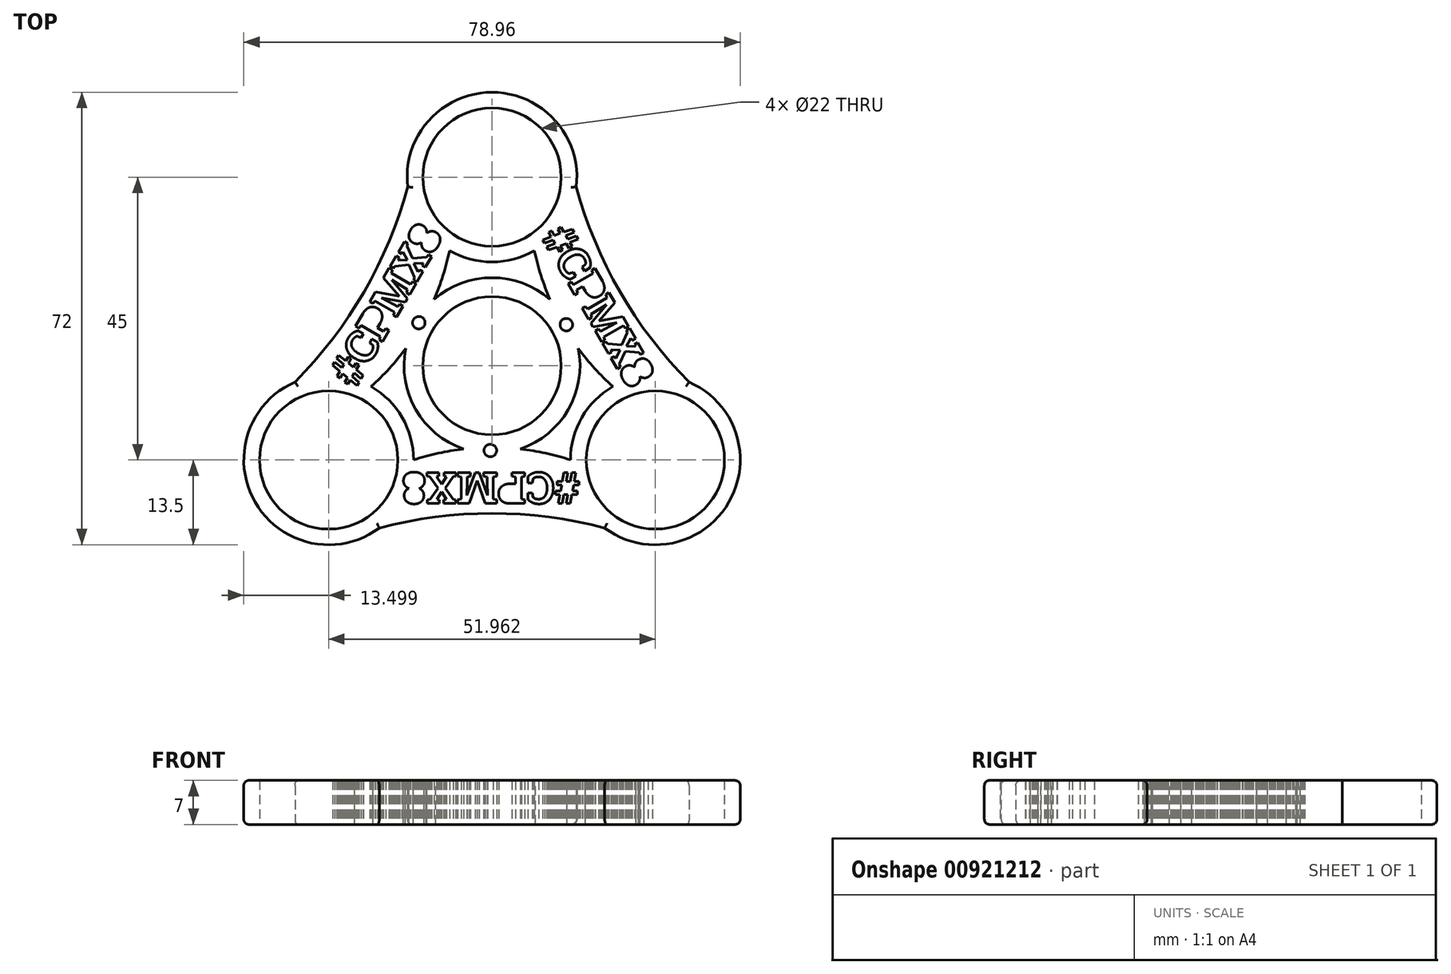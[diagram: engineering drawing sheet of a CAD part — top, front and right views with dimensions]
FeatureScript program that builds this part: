
annotation { "Feature Type Name" : "Feature", "Feature Type Description" : "" }
export const myFeature = defineFeature(function(context is Context, id is Id, definition is map)
    precondition{}
    {
        {
            var Q0;
            Q0=qCreatedBy(makeId("Top.planeOp"),FACE);
            var sketch = newSketch(context, id + "F0", { "sketchPlane" : qUnion([Q0])});
            skCircle(sketch, "E0", {"center": v(0, 0) * mm, "radius": 11 * mm});
            skLineSegment(sketch, "E1", {"start": v(0, 0) * mm, "end": v(0, 30) * mm, "construction": true});
            skCircle(sketch, "E2", {"center": v(0, 30) * mm, "radius": 11 * mm});
            skCircle(sketch, "E3.1.0", {"center": v(-25.98, -15) * mm, "radius": 11 * mm});
            skCircle(sketch, "E3.2.0", {"center": v(25.98, -15) * mm, "radius": 11 * mm});
            skArc(sketch, "E4.0", {"start": v(-31.34, -2.6) * mm, "mid": v(-37.67, -21.75) * mm, "end": v(-17.93, -25.83) * mm});
            skArc(sketch, "E5.0", {"start": v(-6.75, 18.3) * mm, "mid": v(0, 16.5) * mm, "end": v(6.75, 18.3) * mm});
            skArc(sketch, "E6.0", {"start": v(19.23, -3.3) * mm, "mid": v(14.29, -8.25) * mm, "end": v(12.48, -15) * mm});
            skArc(sketch, "E7.0", {"start": v(-13.73, 2.73) * mm, "mid": v(-12.12, -7) * mm, "end": v(-4.5, -13.26) * mm});
            skLineSegment(sketch, "E8", {"start": v(25.98, -15) * mm, "end": v(0, 30) * mm, "construction": true});
            skLineSegment(sketch, "E9", {"start": v(0, 30) * mm, "end": v(-25.98, -15) * mm, "construction": true});
            skArc(sketch, "E10", {"start": v(-31.34, -2.6) * mm, "mid": v(-20.35, 11.75) * mm, "end": v(-13.4, 28.44) * mm});
            skArc(sketch, "E11", {"start": v(17.93, -25.83) * mm, "mid": v(0, -23.5) * mm, "end": v(-17.93, -25.83) * mm});
            skArc(sketch, "E12", {"start": v(13.4, 28.44) * mm, "mid": v(20.35, 11.75) * mm, "end": v(31.34, -2.6) * mm});
            skPoint(sketch, "E13.orphan", {"position": v(-11.7, 36.75) * mm});
            skPoint(sketch, "E14.orphan", {"position": v(-37.67, -8.25) * mm});
            skPoint(sketch, "E15.orphan", {"position": v(11.7, 36.75) * mm});
            skPoint(sketch, "E16.orphan", {"position": v(37.67, -8.25) * mm});
            skPoint(sketch, "E17.end.orphan", {"position": v(25.98, -28.5) * mm});
            skPoint(sketch, "E17.start.orphan", {"position": v(-25.98, -28.5) * mm});
            skArc(sketch, "E18", {"start": v(-19.23, -3.3) * mm, "mid": v(-16.33, -0.43) * mm, "end": v(-13.73, 2.73) * mm});
            skArc(sketch, "E19", {"start": v(6.75, 18.3) * mm, "mid": v(7.8, 14.35) * mm, "end": v(9.23, 10.53) * mm});
            skArc(sketch, "E20.trimOffspring", {"start": v(9.23, 10.53) * mm, "mid": v(0, 14) * mm, "end": v(-9.23, 10.53) * mm});
            skArc(sketch, "E21", {"start": v(12.48, -15) * mm, "mid": v(8.54, -13.92) * mm, "end": v(4.5, -13.26) * mm});
            skArc(sketch, "E22.trimOffspring", {"start": v(4.5, -13.26) * mm, "mid": v(12.12, -7) * mm, "end": v(13.73, 2.73) * mm});
            skArc(sketch, "E23.trimOffspring", {"start": v(13.4, 28.44) * mm, "mid": v(0, 43.5) * mm, "end": v(-13.4, 28.44) * mm});
            skArc(sketch, "E24.trimOffspring", {"start": v(17.93, -25.83) * mm, "mid": v(37.67, -21.75) * mm, "end": v(31.34, -2.6) * mm});
            skArc(sketch, "E25.trimOffspring", {"start": v(-12.48, -15) * mm, "mid": v(-14.29, -8.25) * mm, "end": v(-19.23, -3.3) * mm});
            skArc(sketch, "E26.trimOffspring", {"start": v(-4.5, -13.26) * mm, "mid": v(-8.54, -13.92) * mm, "end": v(-12.48, -15) * mm});
            skArc(sketch, "E27.trimOffspring", {"start": v(13.73, 2.73) * mm, "mid": v(16.33, -0.43) * mm, "end": v(19.23, -3.3) * mm});
            skArc(sketch, "E28.trimOffspring", {"start": v(-9.23, 10.53) * mm, "mid": v(-7.8, 14.35) * mm, "end": v(-6.75, 18.3) * mm});
            skLineSegment(sketch, "E29", {"start": v(-25.98, -15) * mm, "end": v(25.98, -15) * mm, "construction": true});
            skText(sketch, "E30", { "text": "#CPMX8", "fontName": "RobotoSlab-Bold.ttf"});
            skText(sketch, "E31", { "text": "#CPMX8", "fontName": "RobotoSlab-Bold.ttf"});
            skText(sketch, "E32", { "text": "#CPMX8", "fontName": "RobotoSlab-Bold.ttf"});
            skLineSegment(sketch, "E33", {"start": v(-14.67, 8.58) * mm, "end": v(-11.64, 6.83) * mm, "construction": true});
            skCircle(sketch, "E34", {"center": v(-11.64, 6.83) * mm, "radius": 1 * mm});
            skLineSegment(sketch, "E35", {"start": v(14.85, 8.27) * mm, "end": v(11.82, 6.52) * mm, "construction": true});
            skCircle(sketch, "E36", {"center": v(11.82, 6.52) * mm, "radius": 1 * mm});
            skLineSegment(sketch, "E37", {"start": v(-0.26, -17) * mm, "end": v(-0.26, -13.5) * mm, "construction": true});
            skCircle(sketch, "E38", {"center": v(-0.26, -13.5) * mm, "radius": 1 * mm});
            const initialGuessF0  = {"E30": [-0.0218, -0.00375, 0.5, 0.86603, 0.005], "E31": [0.00773, 0.0206, 0.5, -0.86603, 0.005], "E32": [0.01398, -0.017, -1, 0, 0.005]};
            skSetInitialGuess(sketch, initialGuessF0);
            skSolve(sketch);
        }
        {
            var Q0;
            Q0 = qSketchRegion(id + "F0", true);
            extrude(context, id + "F1", {"entities" : qUnion([Q0]), "depth" : 7 * mm, "offsetDistance" : 25 * mm});
        }
        {
            var Q0;
            Q0=makeQuery(id+"F1.opExtrude","CAP_EDGE",EDGE,{"disambiguationData":[OSD([sQuery(id+"F0.wireOp",EDGE,"E4.0")])],"isStart":false});
            var Q1;
            Q1=makeQuery(id+"F1.opExtrude","CAP_EDGE",EDGE,{"disambiguationData":[OSD([sQuery(id+"F0.wireOp",EDGE,"E11")])],"isStart":false});
            var Q2;
            Q2=makeQuery(id+"F1.opExtrude","CAP_EDGE",EDGE,{"disambiguationData":[OSD([sQuery(id+"F0.wireOp",EDGE,"E24.trimOffspring")])],"isStart":false});
            var Q3;
            Q3=makeQuery(id+"F1.opExtrude","CAP_EDGE",EDGE,{"disambiguationData":[OSD([sQuery(id+"F0.wireOp",EDGE,"E12")])],"isStart":false});
            var Q4;
            Q4=makeQuery(id+"F1.opExtrude","CAP_EDGE",EDGE,{"disambiguationData":[OSD([sQuery(id+"F0.wireOp",EDGE,"E23.trimOffspring")])],"isStart":false});
            var Q5;
            Q5=makeQuery(id+"F1.opExtrude","CAP_EDGE",EDGE,{"disambiguationData":[OSD([sQuery(id+"F0.wireOp",EDGE,"E10")])],"isStart":false});
            var Q6;
            Q6=makeQuery(id+"F1.opExtrude","CAP_EDGE",EDGE,{"disambiguationData":[OSD([sQuery(id+"F0.wireOp",EDGE,"E23.trimOffspring")])],"isStart":true});
            var Q7;
            Q7=makeQuery(id+"F1.opExtrude","CAP_EDGE",EDGE,{"disambiguationData":[OSD([sQuery(id+"F0.wireOp",EDGE,"E10")])],"isStart":true});
            var Q8;
            Q8=makeQuery(id+"F1.opExtrude","CAP_EDGE",EDGE,{"disambiguationData":[OSD([sQuery(id+"F0.wireOp",EDGE,"E4.0")])],"isStart":true});
            var Q9;
            Q9=makeQuery(id+"F1.opExtrude","CAP_EDGE",EDGE,{"disambiguationData":[OSD([sQuery(id+"F0.wireOp",EDGE,"E12")])],"isStart":true});
            var Q10;
            Q10=makeQuery(id+"F1.opExtrude","CAP_EDGE",EDGE,{"disambiguationData":[OSD([sQuery(id+"F0.wireOp",EDGE,"E24.trimOffspring")])],"isStart":true});
            var Q11;
            Q11=makeQuery(id+"F1.opExtrude","CAP_EDGE",EDGE,{"disambiguationData":[OSD([sQuery(id+"F0.wireOp",EDGE,"E11")])],"isStart":true});
            fillet(context, id + "F2", {"entities" : qUnion([Q0, Q1, Q2, Q3, Q4, Q5, Q6, Q7, Q8, Q9, Q10, Q11]), "radius" : 0.8 * mm, "tangentPropagation" : true, "allowEdgeOverflow" : false});
        }
    });
